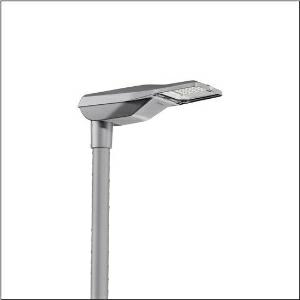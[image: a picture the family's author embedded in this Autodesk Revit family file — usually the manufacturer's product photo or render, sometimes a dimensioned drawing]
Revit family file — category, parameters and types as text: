
# Revit family: streetlight_sl_21_iq_micro___st1_0a_5xe1d41g08cb_d625
name_source: partatom
category: Lighting Fixtures
units: mm (PartAtom-declared; Revit-internal decimal feet)

## family parameters
Cut with Voids When Loaded = No
Host = Face
Light Source = No
Part Type = Normal
Room Calculation Point = No
Round Connector Dimension = Use Diameter
Shared = No

## types (1)
- --- (1 x LED, 2980 lm, 19.4 W, 4000K)
    Apparent Load = 19 VA
    CIE Flux Codes = 37 72 97 100 100
    Color Rendering = 70
    Color Temperature = 4000K
    Default Elevation = 1800 mm
    Description = Streetlight SL 21 iQ micro, mast luminaire, primary light control with lens, of PMMA, primary optical cover: cover, of toughened safety glass, transparent, light distribution: ST1.0a, light emission: direct distribution, primary light characteristic: asymmetric, installation type: post-top, side-entry, LED, High Power LED, rated luminous flux: 2.980lm, luminous efficacy: 154lm/W, light colour: 740, colour temperature: 4000K, control gear: iQ Street-Remote, control: Street-Remote, Auto-Match, Temp-Guard, Lumen-Switch, Night-Set, Smart-Wire, Light-Fading, Desk-Remote (wireless, voltage-free reading and setting of iQ features in the workshop via application-optimized NFC function/RFID function), optimised constant luminous flux control (CLO 2.0), pre-setting: linear dimming characteristic, mains connection: 220..240V, AC, 50/60Hz, start of lifetime: 19W, end of service life: 20W, reduction: 10W, luminaire housing, of diecast aluminium, powder-coated, Siteco® metallic grey (DB 702S), corrosivity category C5 mid according to DIN EN ISO 12944, please order mast flange separately, inclination adjustable: 0°, 5°, 10°, 15°, sealing non-destructively replaceable, multi-level sealing system, length: 528mm, width: 235mm, height: 110mm, mast flange for spigot size: 42mm (side-entry): 5XC10008XM4, 60/48mm (side-entry/post-top): 5XC10108XM2, 76/60mm (side-entry/post-top): 5XC10108XM1, protection rating (complete): IP66, insulation class (complete): insulation class II (safety insulation), certification: CE, ENEC, ENEC+, VDE, impact resistance: IK10, permissible operating ambient temperature for outdoor applications: -40..+50°C, standard-compliant lighting for roads and squares, packaging unit: 1 piece

Light Distribution: ST1.0a
    Height = 110 mm
    Lamp = 1 x LED
    Lamp Light Flux = 2980 lm
    Lamp Power = 19.4 W
    Lamp count = 1
    Length = 528 mm
    Luminous efficacy = 154 lm/W
    Manufacturer = Siteco
    ModVariant = No
    Model = 5XE1D41G08CB
    Number of Poles = 1
    OnlyDefault = Yes
    Power Factor = 1
    Product Name = Streetlight SL 21 iQ micro | ST1.0a
    Product group = mast luminaire | pylon top
    ProductGroupID = 6100
    Protection Class = Protection class II
    Protection Degree = IP 66
    RLX_Detail_Level = 1
    RLX_Emergency_Light_Flux = 0 lm
    RLX_Emergency_Type = 0
    RLX_Emergency_Type_DB = No
    RlxData = <blob elided: 98505 chars, md5=8749e1a5>
    Socket = socket
    Standby Power = 0 W
    System Light Flux = 2980 lm
    System Power = 19 W
    Type Comments = factory setting: luminous flux: 100 % | dim-lin: 254 | 387 mA
    Type Image = l_1006881.jpg
    URL = http://relux.com
    VarID = @adj_160659
    Voltage = 0 V
    Weight = 0.00 kg
    Width = 235 mm

## geometry (parser evidence)
native form markers: Blend x4, Sweep x11
no freeform markers — native parametric forms only
